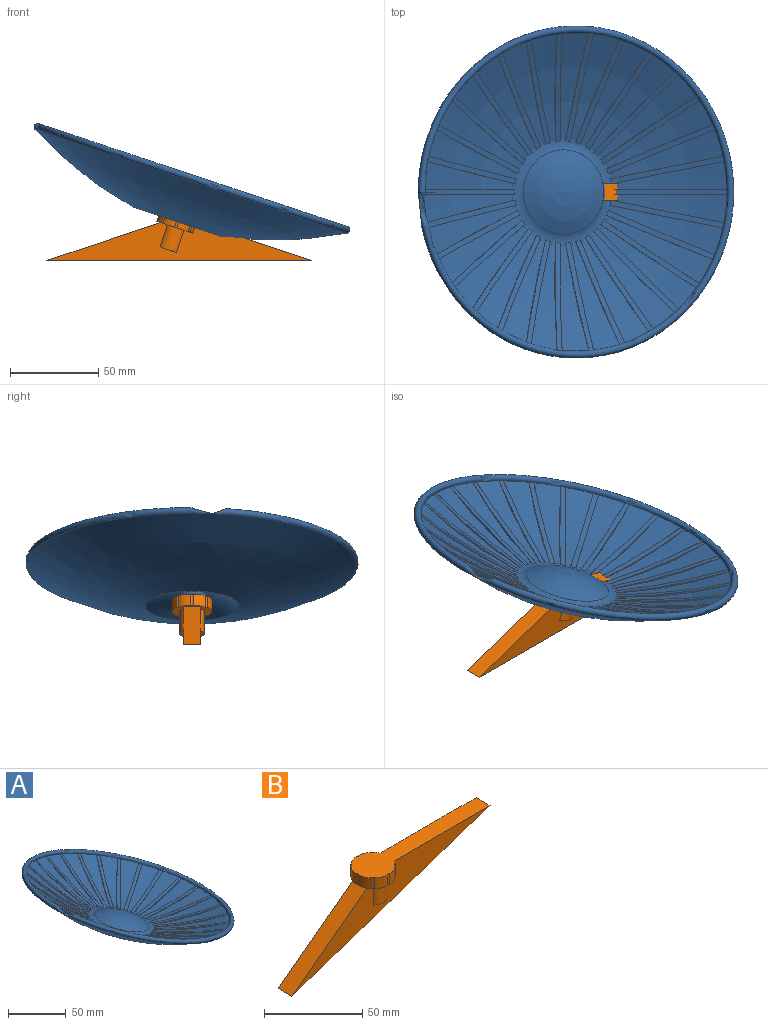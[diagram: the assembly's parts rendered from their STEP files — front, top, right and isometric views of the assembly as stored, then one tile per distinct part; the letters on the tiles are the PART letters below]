
ASSEMBLY  parts=2 mates=1
PART A: 148 faces, bbox 192.9x205.2x73.5 mm
  f0: cone r=4mm half-angle=45deg, axis (0.34,0,0.94), area 48.4mm2, adj f1,f2,f3,f4,f5,f126,f127,f136
  f1: cylinder r=4mm len=8.85mm, axis (-0.34,0,-0.94), area 20.7mm2, adj f0,f128,f144,f147
  f2: cylinder r=4mm len=8.85mm, axis (-0.34,0,-0.94), area 20.7mm2, adj f0,f128,f136,f145
  f3: cylinder r=4mm len=8.85mm, axis (-0.34,0,-0.94), area 20.7mm2, adj f0,f128,f138,f143
  f4: cylinder r=4mm len=8.85mm, axis (-0.34,0,-0.94), area 20.7mm2, adj f0,f128,f141,f142
  f5: cylinder r=4mm len=9.23mm, axis (-0.34,0,-0.94), area 20.7mm2, adj f0,f128,f139,f146
  f6: revolved ~64.6x30.48mm, area 585.5mm2, adj f7,f9,f11,f12,f123,f132
  f7: cylinder r=354.96mm len=64.84mm, axis (0.2,0.98,-0.07), area 196.7mm2, adj f6,f8,f9,f124,f132
  f8: plane 65.19x13.81mm, normal (0.2,0.98,-0.07), area 44.7mm2, adj f7,f124,f132
  f9: plane 65.28x13.83mm, normal (-0.2,-0.98,0.07), area 44.7mm2, adj f6,f7,f132
  f10: revolved ~62.11x40.8mm, area 585.5mm2, adj f11,f13,f15,f16,f123,f132
  f11: cylinder r=354.96mm len=61.66mm, axis (0.38,0.91,-0.14), area 196.7mm2, adj f6,f10,f12,f13,f132
  f12: plane 61.45x26.03mm, normal (0.38,0.91,-0.14), area 44.7mm2, adj f6,f11,f132
  f13: plane 61.55x26.07mm, normal (-0.38,-0.91,0.14), area 44.7mm2, adj f10,f11,f132
  f14: revolved ~57.23x49.34mm, area 585.5mm2, adj f15,f17,f19,f20,f123,f132
  f15: cylinder r=354.96mm len=56.13mm, axis (0.55,0.81,-0.2), area 196.7mm2, adj f10,f14,f16,f17,f132
  f16: plane 55.41x37.16mm, normal (0.55,0.81,-0.2), area 44.7mm2, adj f10,f15,f132
  f17: plane 55.5x37.22mm, normal (-0.55,-0.81,0.2), area 44.7mm2, adj f14,f15,f132
  f18: revolved ~55.72x50.18mm, area 585.5mm2, adj f19,f21,f23,f24,f123,f132
  f19: cylinder r=354.96mm len=48.47mm, axis (0.7,0.67,-0.25), area 196.7mm2, adj f14,f18,f20,f21,f132
  f20: plane 47.33x46.71mm, normal (0.7,0.67,-0.25), area 44.7mm2, adj f14,f19,f132
  f21: plane 47.41x46.78mm, normal (-0.7,-0.67,0.25), area 44.7mm2, adj f18,f19,f132
  f22: revolved ~59.66x41.28mm, area 585.5mm2, adj f23,f25,f27,f28,f123,f132
  f23: cylinder r=354.96mm len=54.82mm, axis (0.81,0.5,-0.3), area 196.7mm2, adj f18,f22,f24,f25,f132
  f24: plane 54.27x37.56mm, normal (0.81,0.5,-0.3), area 44.7mm2, adj f18,f23,f132
  f25: plane 54.34x37.62mm, normal (-0.81,-0.5,0.3), area 44.7mm2, adj f22,f23,f132
  f26: revolved ~61x30.9mm, area 585.5mm2, adj f27,f29,f31,f32,f123,f132
  f27: cylinder r=354.96mm len=59.48mm, axis (0.89,0.31,-0.33), area 196.7mm2, adj f22,f26,f28,f29,f132
  f28: plane 59.5x26.53mm, normal (0.89,0.31,-0.33), area 44.7mm2, adj f22,f27,f132
  f29: plane 59.58x26.57mm, normal (-0.89,-0.31,0.33), area 44.7mm2, adj f26,f27,f132
  f30: revolved ~60.16x25.21mm, area 585.5mm2, adj f31,f33,f35,f36,f123,f132
  f31: cylinder r=354.96mm len=61.54mm, axis (0.93,0.1,-0.34), area 196.7mm2, adj f26,f30,f32,f33,f132
  f32: plane 62.17x19.86mm, normal (0.93,0.1,-0.34), area 44.7mm2, adj f26,f31,f132
  f33: plane 62.26x20.01mm, normal (-0.93,-0.1,0.34), area 44.7mm2, adj f30,f31,f132
  f34: revolved ~61x29.36mm, area 585.5mm2, adj f35,f37,f39,f40,f123,f132
  f35: cylinder r=354.96mm len=61.54mm, axis (0.93,-0.1,-0.34), area 196.7mm2, adj f30,f34,f36,f37,f132
  f36: plane 62.17x24.25mm, normal (0.93,-0.1,-0.34), area 44.7mm2, adj f30,f35,f132
  f37: plane 62.26x24.3mm, normal (-0.93,0.1,0.34), area 44.7mm2, adj f34,f35,f132
  f38: revolved ~59.66x33.13mm, area 585.5mm2, adj f39,f41,f43,f44,f123,f132
  f39: cylinder r=354.96mm len=59.48mm, axis (0.89,-0.31,-0.33), area 196.7mm2, adj f34,f38,f40,f41,f132
  f40: plane 59.5x28.55mm, normal (0.89,-0.31,-0.33), area 44.7mm2, adj f34,f39,f132
  f41: plane 59.58x28.6mm, normal (-0.89,0.31,0.33), area 44.7mm2, adj f38,f39,f132
  f42: revolved ~55.72x36.38mm, area 585.5mm2, adj f43,f45,f47,f48,f123,f132
  f43: cylinder r=354.96mm len=54.82mm, axis (0.81,-0.5,-0.3), area 196.7mm2, adj f38,f42,f44,f45,f132
  f44: plane 54.27x32.57mm, normal (0.81,-0.5,-0.3), area 44.7mm2, adj f38,f43,f132
  f45: plane 54.34x32.62mm, normal (-0.81,0.5,0.3), area 44.7mm2, adj f42,f43,f132
  f46: revolved ~49.34x42.03mm, area 585.5mm2, adj f47,f49,f51,f52,f123,f132
  f47: cylinder r=354.96mm len=47.76mm, axis (0.7,-0.67,-0.25), area 196.7mm2, adj f42,f46,f48,f49,f132
  f48: plane 46.71x36.12mm, normal (0.7,-0.67,-0.25), area 44.7mm2, adj f42,f47,f132
  f49: plane 46.78x36.18mm, normal (-0.7,0.67,0.25), area 44.7mm2, adj f46,f47,f132
  f50: revolved ~46.91x40.8mm, area 585.5mm2, adj f51,f53,f55,f56,f123,f132
  f51: cylinder r=354.96mm len=40.79mm, axis (0.55,-0.81,-0.2), area 196.7mm2, adj f46,f50,f52,f53,f132
  f52: plane 40.11x39.06mm, normal (0.55,-0.81,-0.2), area 44.7mm2, adj f46,f51,f132
  f53: plane 40.16x39.13mm, normal (-0.55,0.81,0.2), area 44.7mm2, adj f50,f51,f132
  f54: revolved ~49.4x41.62mm, area 585.5mm2, adj f55,f57,f59,f60,f123,f132
  f55: cylinder r=354.96mm len=46.33mm, axis (0.38,-0.91,-0.14), area 196.7mm2, adj f50,f54,f56,f57,f132
  f56: plane 46.15x41.26mm, normal (0.38,-0.91,-0.14), area 44.7mm2, adj f50,f55,f132
  f57: plane 46.21x41.33mm, normal (-0.38,0.91,0.14), area 44.7mm2, adj f54,f55,f132
  f58: revolved ~49.41x41.63mm, area 585.5mm2, adj f59,f61,f63,f64,f123,f132
  f59: cylinder r=354.96mm len=49.51mm, axis (0.2,-0.98,-0.07), area 196.7mm2, adj f54,f58,f60,f61,f132
  f60: plane 49.88x42.62mm, normal (0.2,-0.98,-0.07), area 44.7mm2, adj f54,f59,f132
  f61: plane 49.95x42.69mm, normal (-0.2,0.98,0.07), area 44.7mm2, adj f58,f59,f132
  f62: revolved ~49.41x41.63mm, area 585.5mm2, adj f63,f65,f67,f68,f123,f132
  f63: cylinder r=354.96mm len=50.19mm, axis (0,-1,0), area 196.7mm2, adj f58,f62,f64,f65,f132
  f64: plane 51.15x43.08mm, normal (0,-1,0), area 44.7mm2, adj f58,f63,f132
  f65: plane 51.21x43.15mm, normal (0,1,0), area 44.7mm2, adj f62,f63,f132
  f66: revolved ~49.4x41.62mm, area 585.5mm2, adj f67,f69,f71,f72,f123,f132
  f67: cylinder r=354.96mm len=49.51mm, axis (-0.2,-0.98,0.07), area 196.7mm2, adj f62,f66,f68,f69,f132
  f68: plane 49.88x42.62mm, normal (-0.2,-0.98,0.07), area 44.7mm2, adj f62,f67,f132
  f69: plane 49.95x42.69mm, normal (0.2,0.98,-0.07), area 44.7mm2, adj f66,f67,f132
  f70: revolved ~46.91x40.8mm, area 585.5mm2, adj f71,f73,f75,f76,f123,f132
  f71: cylinder r=354.96mm len=46.33mm, axis (-0.38,-0.91,0.14), area 196.7mm2, adj f66,f70,f72,f73,f132
  f72: plane 46.15x41.26mm, normal (-0.38,-0.91,0.14), area 44.7mm2, adj f66,f71,f132
  f73: plane 46.21x41.33mm, normal (0.38,0.91,-0.14), area 44.7mm2, adj f70,f71,f132
  f74: revolved ~49.34x42.03mm, area 585.5mm2, adj f75,f77,f79,f80,f123,f132
  f75: cylinder r=354.96mm len=40.79mm, axis (-0.55,-0.81,0.2), area 196.7mm2, adj f70,f74,f76,f77,f132
  f76: plane 40.11x39.06mm, normal (-0.55,-0.81,0.2), area 44.7mm2, adj f70,f75,f132
  f77: plane 40.16x39.13mm, normal (0.55,0.81,-0.2), area 44.7mm2, adj f74,f75,f132
  f78: revolved ~55.72x36.38mm, area 585.5mm2, adj f79,f81,f83,f84,f123,f132
  f79: cylinder r=354.96mm len=47.76mm, axis (-0.7,-0.67,0.25), area 196.7mm2, adj f74,f78,f80,f81,f132
  f80: plane 46.71x36.12mm, normal (-0.7,-0.67,0.25), area 44.7mm2, adj f74,f79,f132
  f81: plane 46.78x36.18mm, normal (0.7,0.67,-0.25), area 44.7mm2, adj f78,f79,f132
  f82: revolved ~59.66x33.13mm, area 585.5mm2, adj f83,f85,f87,f88,f123,f132
  f83: cylinder r=354.96mm len=54.82mm, axis (-0.81,-0.5,0.3), area 196.7mm2, adj f78,f82,f84,f85,f132
  f84: plane 54.27x32.57mm, normal (-0.81,-0.5,0.3), area 44.7mm2, adj f78,f83,f132
  f85: plane 54.34x32.62mm, normal (0.81,0.5,-0.3), area 44.7mm2, adj f82,f83,f132
  f86: revolved ~61x29.36mm, area 585.5mm2, adj f87,f89,f91,f92,f123,f132
  f87: cylinder r=354.96mm len=59.48mm, axis (-0.89,-0.31,0.33), area 196.7mm2, adj f82,f86,f88,f89,f132
  f88: plane 59.5x28.55mm, normal (-0.89,-0.31,0.33), area 44.7mm2, adj f82,f87,f132
  f89: plane 59.58x28.6mm, normal (0.89,0.31,-0.33), area 44.7mm2, adj f86,f87,f132
  f90: revolved ~60.16x25.21mm, area 585.5mm2, adj f91,f93,f95,f96,f123,f132
  f91: cylinder r=354.96mm len=61.54mm, axis (-0.93,-0.1,0.34), area 196.7mm2, adj f86,f90,f92,f93,f132
  f92: plane 62.17x24.25mm, normal (-0.93,-0.1,0.34), area 44.7mm2, adj f86,f91,f132
  f93: plane 62.26x24.3mm, normal (0.93,0.1,-0.34), area 44.7mm2, adj f90,f91,f132
  f94: revolved ~61x30.9mm, area 585.5mm2, adj f95,f97,f99,f100,f123,f132
  f95: cylinder r=354.96mm len=61.54mm, axis (-0.93,0.1,0.34), area 196.7mm2, adj f90,f94,f96,f97,f132
  f96: plane 62.17x19.86mm, normal (-0.93,0.1,0.34), area 44.7mm2, adj f90,f95,f132
  f97: plane 62.26x20.01mm, normal (0.93,-0.1,-0.34), area 44.7mm2, adj f94,f95,f132
  f98: revolved ~59.66x41.28mm, area 585.5mm2, adj f99,f101,f103,f104,f123,f132
  f99: cylinder r=354.96mm len=59.48mm, axis (-0.89,0.31,0.33), area 196.7mm2, adj f94,f98,f100,f101,f132
  f100: plane 59.5x26.53mm, normal (-0.89,0.31,0.33), area 44.7mm2, adj f94,f99,f132
  f101: plane 59.58x26.57mm, normal (0.89,-0.31,-0.33), area 44.7mm2, adj f98,f99,f132
  f102: revolved ~55.72x50.18mm, area 585.5mm2, adj f103,f105,f107,f108,f123,f132
  f103: cylinder r=354.96mm len=54.82mm, axis (-0.81,0.5,0.3), area 196.7mm2, adj f98,f102,f104,f105,f132
  f104: plane 54.27x37.56mm, normal (-0.81,0.5,0.3), area 44.7mm2, adj f98,f103,f132
  f105: plane 54.34x37.62mm, normal (0.81,-0.5,-0.3), area 44.7mm2, adj f102,f103,f132
  f106: revolved ~57.23x49.34mm, area 585.5mm2, adj f107,f109,f111,f112,f123,f132
  f107: cylinder r=354.96mm len=48.47mm, axis (-0.7,0.67,0.25), area 196.7mm2, adj f102,f106,f108,f109,f132
  f108: plane 47.33x46.71mm, normal (-0.7,0.67,0.25), area 44.7mm2, adj f102,f107,f132
  f109: plane 47.41x46.78mm, normal (0.7,-0.67,-0.25), area 44.7mm2, adj f106,f107,f132
  f110: revolved ~62.11x40.8mm, area 585.5mm2, adj f111,f113,f115,f116,f123,f132
  f111: cylinder r=354.96mm len=56.13mm, axis (-0.55,0.81,0.2), area 196.7mm2, adj f106,f110,f112,f113,f132
  f112: plane 55.41x37.16mm, normal (-0.55,0.81,0.2), area 44.7mm2, adj f106,f111,f132
  f113: plane 55.5x37.22mm, normal (0.55,-0.81,-0.2), area 44.7mm2, adj f110,f111,f132
  f114: revolved ~64.6x30.48mm, area 585.5mm2, adj f115,f117,f119,f120,f123,f132
  f115: cylinder r=354.96mm len=61.66mm, axis (-0.38,0.91,0.14), area 196.7mm2, adj f110,f114,f116,f117,f132
  f116: plane 61.45x26.03mm, normal (-0.38,0.91,0.14), area 44.7mm2, adj f110,f115,f132
  f117: plane 61.55x26.07mm, normal (0.38,-0.91,-0.14), area 44.7mm2, adj f114,f115,f132
  f118: revolved ~64.61x18.83mm, area 585.5mm2, adj f119,f121,f123,f132,f133,f134
  f119: cylinder r=354.96mm len=64.84mm, axis (-0.2,0.98,0.07), area 196.7mm2, adj f114,f118,f120,f121,f132
  f120: plane 65.19x13.81mm, normal (-0.2,0.98,0.07), area 44.7mm2, adj f114,f119,f132
  f121: plane 65.28x13.83mm, normal (0.2,-0.98,-0.07), area 44.7mm2, adj f118,f119,f132
  f122: revolved ~186.6x175.35mm, area 27145.3mm2, adj f123,f131
  f123: torus R=92.32mm, axis (-0.34,0,-0.94), area 5471.8mm2, adj f6,f10,f14,f18,f22,f26,f30,f34
  f124: revolved ~64.61x18.83mm, area 585.5mm2, adj f7,f8,f123,f132,f134,f135
  f125: sphere r=53.78mm, area 1916.1mm2, adj f132
  f126: plane 4x3.76mm, normal (-0.34,0,-0.94), area 12.6mm2, adj f0
  f127: cylinder r=4mm len=9.23mm, axis (-0.34,0,-0.94), area 20.7mm2, adj f0,f128,f137,f140
  f128: plane 13.17x12.38mm, normal (-0.34,0,-0.94), area 89.8mm2, adj f1,f2,f3,f4,f5,f127,f129,f136
  f129: cone r=8mm half-angle=45deg, axis (0.34,0,0.94), area 91.6mm2, adj f128,f130
  f130: cylinder r=8mm len=16mm, axis (-0.34,0,-0.94), area 98.7mm2, adj f129,f131
  f131: sphere r=51.78mm, area 2189mm2, adj f122,f130
  f132: torus R=28.51mm, axis (-0.34,0,-0.94), area 1010.7mm2, adj f6,f7,f8,f9,f10,f11,f12,f13
  f133: plane 66.45x3.59mm, normal (0,1,0), area 44.7mm2, adj f118,f132,f134
  f134: cylinder r=354.96mm len=65.52mm, axis (0,1,0), area 196.7mm2, adj f118,f124,f132,f133,f135
  f135: plane 66.55x3.79mm, normal (0,-1,0), area 44.7mm2, adj f124,f132,f134
  f136: plane 9.55x4.2mm, normal (0,-1,0), area 10.1mm2, adj f0,f2,f128,f137
  f137: plane 9.18x3.92mm, normal (-0.81,-0.5,0.3), area 10.1mm2, adj f0,f127,f128,f136
  f138: plane 9.18x4.42mm, normal (0,1,0), area 10.1mm2, adj f0,f3,f128,f139
  f139: plane 9.36x3.69mm, normal (0.81,0.5,-0.3), area 10.1mm2, adj f0,f5,f128,f138
  f140: plane 9.36x3.69mm, normal (0.81,-0.5,-0.3), area 10.1mm2, adj f0,f127,f128,f141
  f141: plane 9.18x4.42mm, normal (0,-1,0), area 10.1mm2, adj f0,f4,f128,f140
  f142: plane 9.18x3.92mm, normal (0.81,0.5,-0.3), area 10.1mm2, adj f0,f4,f128,f143
  f143: plane 9.18x3.92mm, normal (0.81,-0.5,-0.3), area 10.1mm2, adj f0,f3,f128,f142
  f144: plane 9.36x3.69mm, normal (-0.81,-0.5,0.3), area 10.1mm2, adj f0,f1,f128,f145
  f145: plane 9.36x3.69mm, normal (-0.81,0.5,0.3), area 10.1mm2, adj f0,f2,f128,f144
  f146: plane 9.18x3.92mm, normal (-0.81,0.5,0.3), area 10.1mm2, adj f0,f5,f128,f147
  f147: plane 9.55x4.2mm, normal (0,1,0), area 10.1mm2, adj f0,f1,f128,f146
PART B: 25 faces, bbox 142.9x22.7x47.6 mm
  f0: cylinder r=11.35mm len=6.7mm, axis (0,0,1), area 20.1mm2, adj f15,f17,f18,f24
  f1: cylinder r=7mm len=13.3mm, axis (0,0,1), area 144.3mm2, adj f2,f17,f24
  f2: plane 9.8x2mm, normal (0,0,-1), area 13.5mm2, adj f1,f24
  f3: cylinder r=1mm len=6.7mm, axis (0,0,1), area 11.1mm2, adj f4,f16,f17,f18
  f4: cylinder r=11.35mm len=6.75mm, axis (0,0,1), area 49.8mm2, adj f3,f5,f17,f18
  f5: cylinder r=1mm len=6.7mm, axis (0,0,1), area 11.1mm2, adj f4,f6,f17,f18
  f6: cylinder r=11.35mm len=6.75mm, axis (0,0,1), area 49.8mm2, adj f5,f7,f17,f18
  f7: cylinder r=1mm len=6.7mm, axis (0,0,1), area 11.1mm2, adj f6,f8,f17,f18
  f8: cylinder r=11.35mm len=6.75mm, axis (0,0,1), area 49.8mm2, adj f7,f9,f17,f18
  f9: cylinder r=1mm len=6.7mm, axis (0,0,1), area 11.1mm2, adj f8,f10,f17,f18
  f10: cylinder r=11.35mm len=6.75mm, axis (0,0,1), area 49.8mm2, adj f9,f11,f17,f18
  f11: cylinder r=1mm len=6.7mm, axis (0,0,1), area 11.1mm2, adj f10,f12,f17,f18
  f12: cylinder r=11.35mm len=6.75mm, axis (0,0,1), area 49.8mm2, adj f11,f13,f17,f18
  f13: cylinder r=1mm len=6.7mm, axis (0,0,1), area 11.1mm2, adj f12,f14,f17,f18
  f14: cylinder r=11.35mm len=6.7mm, axis (0,0,1), area 20.1mm2, adj f13,f17,f18,f23
  f15: cylinder r=1mm len=6.7mm, axis (0,0,1), area 11.1mm2, adj f0,f16,f17,f18
  f16: cylinder r=11.35mm len=6.75mm, axis (0,0,1), area 49.8mm2, adj f3,f15,f17,f18
  f17: plane 22.65x21.52mm, normal (0,0,-1), area 176.2mm2, adj f0,f1,f3,f4,f5,f6,f7,f8
  f18: plane 90.69x22.65mm, normal (0,0,1), area 1086.2mm2, adj f0,f3,f4,f5,f6,f7,f8,f9
  f19: cylinder r=7mm len=13.3mm, axis (0,0,1), area 144.3mm2, adj f17,f20,f23
  f20: plane 9.8x2mm, normal (0,0,-1), area 13.5mm2, adj f19,f23
  f21: plane 54.56x40.92mm, normal (-0.6,0,0.8), area 682mm2, adj f17,f22,f23,f24
  f22: plane 142.86x47.62mm, normal (0.32,0,-0.95), area 1505.9mm2, adj f18,f21,f23,f24
  f23: plane 142.86x47.62mm, normal (0,-1,0), area 1661.3mm2, adj f14,f17,f18,f19,f20,f21,f22
  f24: plane 142.86x47.62mm, normal (0,1,0), area 1661.3mm2, adj f0,f1,f2,f17,f18,f21,f22
PLACE A rot(axis=(0,-1,0),1.6deg) t=(0,0,25.1)mm
PLACE B rot(axis=(0,1,0),18.4deg) t=(0,0,25.1)mm
MATE fastened A.f129 <-> B.f10  axis (-0.32,0,-0.95) through (0,0,25.1)mm
